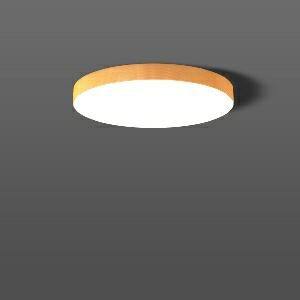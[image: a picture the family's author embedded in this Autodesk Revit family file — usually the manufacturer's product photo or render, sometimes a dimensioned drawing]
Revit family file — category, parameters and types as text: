
# Revit family: flatliner_slim_312287_002_b025
name_source: partatom
category: Lighting Fixtures
units: mm (PartAtom-declared; Revit-internal decimal feet)

## family parameters
Cut with Voids When Loaded = No
Host = Face
Light Source = No
Part Type = Normal
Room Calculation Point = No
Round Connector Dimension = Use Diameter
Shared = No

## types (1)
- 982559.002 (1 x LED Modul 830, 2300 lm, 3000)
    Apparent Load = 29 VA
    CIE Flux Codes = 45 76 94 95 100
    Color Rendering = 80
    Color Temperature = 3000
    Default Elevation = 1800 mm
    Description = Series: FLATLINER SLIM
Decorative ceiling luminaire for interior decoration. Base luminaire prepared for the installation of fabric lampshade. Base: metal, white, powder-coated. Modular design: with the basic luminaire, a cylindrical fabric lampshade with a polycarbonate satin-finish diffuser must always be ordered separately. Fabric lampshade and diffuser can be assembled without the use of tools. 
Colour: white
Diameter: 596 mm
Height: 34 mm
Lamp: LED exchangeable
Socket: without socket
Colour temperature: 3000K
Colour rendering index (CRI): 83
System power: 29 W
Rated luminous flux: 2300 lm
Beam angle Down: 117°
Luminous efficiency: 79 lm/W
Control gear: AC Strom, dim.Ph.an-/abschnitt
Protection class: I
Type of protection: IP 20
    Height = 34 mm  [stored 0.111549 ft]
    Lamp = 1 x LED Modul 830
    Lamp Light Flux = 2300 lm
    Lamp count = 1
    Length = 596 mm
    Lifetime = 50000 h
    Luminous efficacy = 79 lm/W
    Manufacturer = RZB
    ModVariant = No
    Model = 312287.002
    Mounting Place = Ceiling
    Mounting Type = Surface mounted
    Number of Poles = 1
    OnlyDefault = Yes
    Power Factor = 1
    Product Name = FLATLINER SLIM
    Product group = Surface mounted ceiling Fabric lampshade luminaires
    ProductGroupID = 313
    Protection Class = Protection class I
    Protection Degree = IP 20
    RLX_Detail_Level = 1
    RLX_Emergency_Light_Flux = 0 lm
    RLX_Emergency_Type = 0
    RLX_Emergency_Type_DB = No
    RlxData = <blob elided: 23721 chars, md5=81dfac71>
    Socket = socket
    Standby Power = 0 W
    System Light Flux = 2300 lm
    System Power = 29 W
    Type Image = 312287.002_982442.0063_982444.002.jpg
    URL = http://relux.com
    VarID = 982559_002_a29f
    Voltage = 230 V
    Voltage Range = 220-240 V
    Weight = 0.00 kg
    Width = 0 mm  [stored 0 ft]

note: [stored X ft] marks values corroborated as IEEE doubles in the binary element streams (Revit-internal decimal feet)

## geometry (parser evidence)
native form markers: Blend x4, Sweep x15
no freeform markers — native parametric forms only
